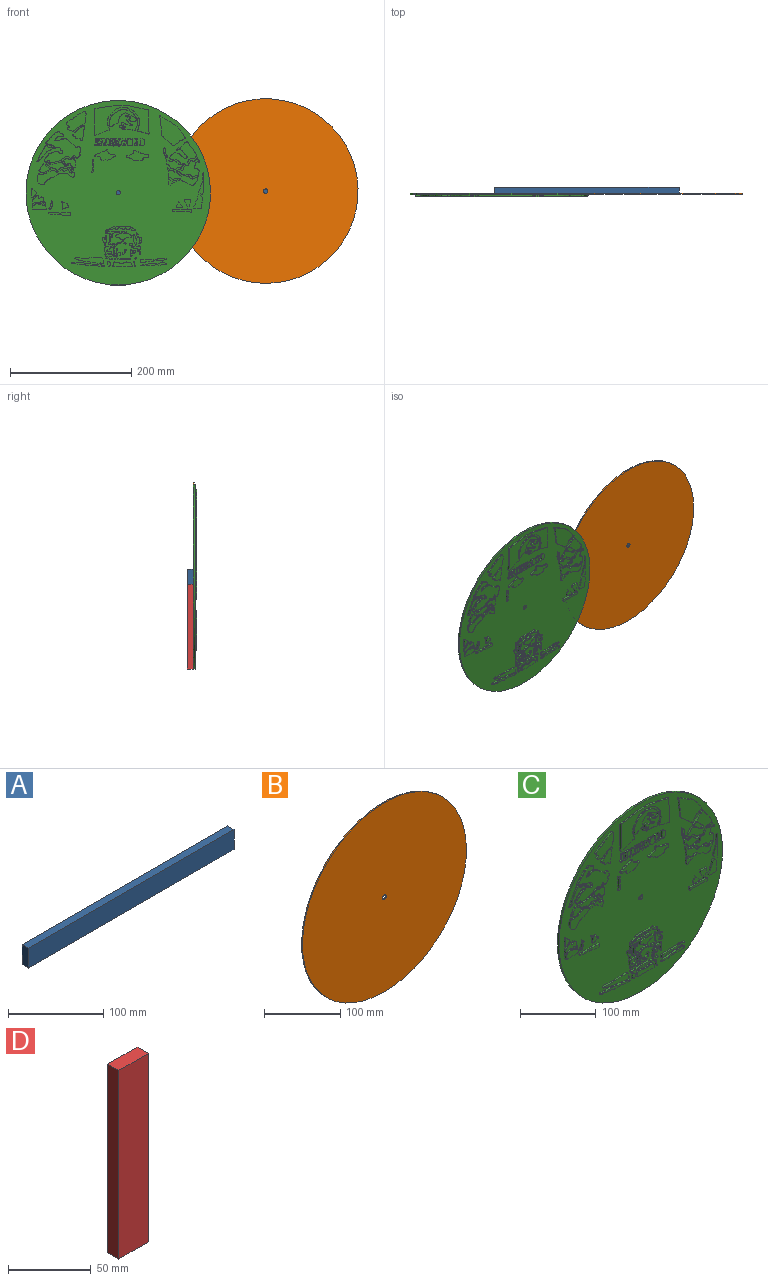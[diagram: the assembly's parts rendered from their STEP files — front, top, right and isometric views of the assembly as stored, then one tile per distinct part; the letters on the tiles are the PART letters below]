
ASSEMBLY  parts=4 mates=5
PART A: 6 faces, bbox 304.8x9.5x25.4 mm
  f0: plane 25.4x9.53mm, normal (1,0,0), area 241.9mm2, adj f1,f3,f4,f5
  f1: plane 304.8x9.53mm, normal (0,0,1), area 2903.2mm2, adj f0,f2,f4,f5
  f2: plane 25.4x9.53mm, normal (-1,0,0), area 241.9mm2, adj f1,f3,f4,f5
  f3: plane 304.8x9.53mm, normal (0,0,-1), area 2903.2mm2, adj f0,f2,f4,f5
  f4: plane 304.8x25.4mm, normal (0,-1,0), area 7741.9mm2, adj f0,f1,f2,f3
  f5: plane 304.8x25.4mm, normal (0,1,0), area 7741.9mm2, adj f0,f1,f2,f3
PART B: 4 faces, bbox 304.8x1.6x304.8 mm
  f0: cylinder r=3.63mm len=7.26mm, axis (0,1,0), area 36.2mm2, adj f2,f3
  f1: cylinder r=152.4mm len=304.8mm, axis (0,1,0), area 1520.1mm2, adj f2,f3
  f2: plane 304.8x304.8mm, normal (0,-1,0), area 72924.4mm2, adj f0,f1
  f3: plane 304.8x304.8mm, normal (0,1,0), area 72924.4mm2, adj f0,f1
PART C: 236 faces, bbox 304.8x5.5x304.8 mm
  f0: cylinder r=3.66mm len=7.32mm, axis (0,1,0), area 67.5mm2, adj f2,f164
  f1: cylinder r=152.4mm len=304.8mm, axis (0,1,0), area 2810.4mm2, adj f2,f164
  f2: plane 304.8x304.8mm, normal (0,1,0), area 72923.8mm2, adj f0,f1
  f3: plane 5.9x3.39mm, normal (-0.87,0,0.5), area 17.3mm2, adj f4,f163,f164,f235
  f4: plane 7.98x6.67mm, normal (0.77,0,0.64), area 26.4mm2, adj f3,f5,f164,f235
  f5: plane 2.54x1.53mm, normal (1,0,0), area 3.9mm2, adj f4,f6,f164,f235
  f6: plane 10.06x2.54mm, normal (0,0,-1), area 25.5mm2, adj f5,f163,f164,f235
  f7: plane 2.73x2.54mm, normal (0.78,0,-0.62), area 8.9mm2, adj f8,f93,f164,f173
  f8: plane 2.73x2.54mm, normal (-1,0,0), area 6.9mm2, adj f7,f9,f164,f173
  f9: plane 2.54x2.05mm, normal (-0.77,0,-0.64), area 6.8mm2, adj f8,f10,f164,f173
  f10: plane 4.07x2.54mm, normal (-0.88,0,-0.48), area 11.8mm2, adj f9,f11,f164,f173
  f11: plane 2.54x1.86mm, normal (-0.77,0,-0.64), area 6.2mm2, adj f10,f12,f164,f173
  f12: plane 4.37x2.54mm, normal (-1,0,0), area 11.1mm2, adj f11,f13,f164,f173
  f13: plane 10.3x2.54mm, normal (0,0,1), area 26.2mm2, adj f12,f14,f164,f173
  f14: plane 5.36x2.54mm, normal (1,0,0), area 13.6mm2, adj f13,f15,f164,f173
  f15: plane 3.28x2.54mm, normal (0.91,0,-0.42), area 9.2mm2, adj f14,f93,f164,f173
  f16: plane 4.25x2.54mm, normal (-0.23,0,0.97), area 11.1mm2, adj f17,f94,f164,f172
  f17: plane 2.54x2.01mm, normal (1,0,0), area 5.1mm2, adj f16,f18,f164,f172
  f18: plane 2.54x1.4mm, normal (-0.25,0,-0.97), area 3.7mm2, adj f17,f19,f164,f172
  f19: plane 3.17x2.54mm, normal (0.36,0,-0.93), area 8.6mm2, adj f18,f20,f164,f172
  f20: plane 2.71x2.54mm, normal (0.42,0,-0.91), area 7.6mm2, adj f19,f21,f164,f172
  f21: plane 5.1x2.78mm, normal (0.48,0,-0.88), area 14.8mm2, adj f20,f22,f164,f172
  f22: plane 2.67x2.54mm, normal (0.64,0,-0.77), area 8.8mm2, adj f21,f23,f164,f172
  f23: plane 2.54x1.97mm, normal (-0.22,0,-0.98), area 5.1mm2, adj f22,f24,f164,f172
  f24: plane 2.54x0.99mm, normal (-0.62,0,-0.78), area 3.2mm2, adj f23,f25,f164,f172
  f25: plane 9.26x2.54mm, normal (-1,0,0), area 23.5mm2, adj f24,f26,f164,f172
  f26: plane 2.54x2.4mm, normal (0.25,0,0.97), area 6.3mm2, adj f25,f27,f164,f172
  f27: plane 2.54x1.35mm, normal (0.77,0,0.64), area 4.5mm2, adj f26,f28,f164,f172
  f28: plane 3.04x2.54mm, normal (0.62,0,0.78), area 9.9mm2, adj f27,f29,f164,f172
  f29: plane 2.54x1.39mm, normal (-0.64,0,0.77), area 4.6mm2, adj f28,f30,f164,f172
  f30: plane 3.3x2.54mm, normal (-0.25,0,0.97), area 8.7mm2, adj f29,f94,f164,f172
  f31: extruded ~11.37x6.92mm, area 47.7mm2, adj f32,f95,f164,f171
  f32: plane 11.22x2.54mm, normal (-1,0,0), area 28.5mm2, adj f31,f95,f164,f171
  f33: plane 11.15x2.54mm, normal (-1,0,0), area 28.3mm2, adj f34,f157,f164,f170
  f34: plane 2.54x2.08mm, normal (0,0,1), area 5.3mm2, adj f33,f35,f164,f170
  f35: plane 8.96x2.54mm, normal (1,0,0), area 22.7mm2, adj f34,f36,f164,f170
  f36: plane 4.28x2.54mm, normal (0,0,1), area 10.9mm2, adj f35,f37,f164,f170
  f37: plane 2.54x2.19mm, normal (1,0,0), area 5.6mm2, adj f36,f157,f164,f170
  f38: plane 11.65x2.54mm, normal (-1,0,0), area 29.6mm2, adj f39,f158,f164,f169
  f39: plane 3.17x2.54mm, normal (0,0,1), area 8mm2, adj f38,f40,f164,f169
  f40: extruded ~6.75x2.78mm, area 21.1mm2, adj f39,f41,f164,f169
  f41: plane 2.54x1.4mm, normal (0.99,0,0.16), area 3.6mm2, adj f40,f42,f164,f169
  f42: plane 3.16x2.54mm, normal (0.97,0,0.25), area 8.3mm2, adj f41,f43,f164,f169
  f43: plane 2.54x1.04mm, normal (0.33,0,-0.94), area 2.8mm2, adj f42,f44,f164,f169
  f44: plane 2.54x0.52mm, normal (0.38,0,-0.93), area 1.4mm2, adj f43,f45,f164,f169
  f45: plane 3.29x2.54mm, normal (-0.93,0,-0.38), area 9mm2, adj f44,f46,f164,f169
  f46: plane 2.54x0.36mm, normal (0,0,-1), area 0.9mm2, adj f45,f47,f164,f169
  f47: plane 2.54x0.18mm, normal (0.68,0,-0.73), area 0.6mm2, adj f46,f48,f164,f169
  f48: plane 2.54x0.41mm, normal (0.9,0,-0.43), area 1.1mm2, adj f47,f49,f164,f169
  f49: plane 2.54x2.48mm, normal (1,0,0.06), area 6.3mm2, adj f48,f158,f164,f169
  f50: plane 11.36x2.57mm, normal (-0.98,0,-0.22), area 29.6mm2, adj f51,f159,f164,f168
  f51: plane 2.54x2.41mm, normal (-0.13,0,0.99), area 6.2mm2, adj f50,f52,f164,f168
  f52: plane 4.78x2.54mm, normal (0.97,0,0.22), area 12.4mm2, adj f51,f53,f164,f168
  f53: plane 2.54x0.24mm, normal (0.89,0,0.46), area 0.7mm2, adj f52,f54,f164,f168
  f54: plane 2.54x0.16mm, normal (-0.21,0,0.98), area 0.4mm2, adj f53,f55,f164,f168
  f55: plane 2.67x2.54mm, normal (-0.98,0,0.21), area 6.9mm2, adj f54,f56,f164,f168
  f56: plane 2.54x2.16mm, normal (0,0,1), area 5.5mm2, adj f55,f57,f164,f168
  f57: plane 2.67x2.54mm, normal (0.97,0,0.22), area 7mm2, adj f56,f58,f164,f168
  f58: plane 2.54x0.2mm, normal (0.4,0,0.92), area 0.6mm2, adj f57,f59,f164,f168
  f59: plane 2.54x0.18mm, normal (-0.92,0,0.4), area 0.5mm2, adj f58,f60,f164,f168
  f60: plane 4.97x2.54mm, normal (-0.97,0,0.22), area 13mm2, adj f59,f61,f164,f168
  f61: plane 2.54x2.31mm, normal (0.22,0,0.97), area 6mm2, adj f60,f62,f164,f168
  f62: plane 11.19x2.58mm, normal (0.97,0,-0.22), area 29.2mm2, adj f61,f63,f164,f168
  f63: plane 2.54x1mm, normal (-0.02,0,-1), area 2.5mm2, adj f62,f64,f164,f168
  f64: plane 2.54x0.18mm, normal (0.24,0,-0.97), area 0.5mm2, adj f63,f65,f164,f168
  f65: plane 2.54x0.83mm, normal (0,0,-1), area 2.1mm2, adj f64,f66,f164,f168
  f66: plane 3.74x2.54mm, normal (-0.98,0,-0.2), area 9.7mm2, adj f65,f67,f164,f168
  f67: plane 2.54x0.2mm, normal (0,0,-1), area 0.5mm2, adj f66,f68,f164,f168
  f68: plane 3.76x2.54mm, normal (0.97,0,-0.23), area 9.8mm2, adj f67,f159,f164,f168
  f69: plane 2.54x2.46mm, normal (0,0,-1), area 6.2mm2, adj f70,f160,f164,f167
  f70: plane 11.34x2.54mm, normal (-1,0,0), area 28.8mm2, adj f69,f71,f164,f167
  f71: plane 2.54x2.46mm, normal (0,0,1), area 6.2mm2, adj f70,f160,f164,f167
  f72: plane 6.45x3.83mm, normal (-0.51,0,-0.86), area 19mm2, adj f73,f161,f164,f166
  f73: plane 2.54x1.64mm, normal (-1,0,-0.07), area 4.2mm2, adj f72,f74,f164,f166
  f74: plane 9.62x3.28mm, normal (-0.95,0,0.32), area 25.8mm2, adj f73,f75,f164,f166
  f75: plane 5.25x2.54mm, normal (-0.94,0,0.35), area 14.2mm2, adj f74,f76,f164,f166
  f76: plane 6.56x2.54mm, normal (-1,0,0), area 16.7mm2, adj f75,f77,f164,f166
  f77: plane 4.92x2.54mm, normal (-0.97,0,0.25), area 12.9mm2, adj f76,f78,f164,f166
  f78: plane 4.18x2.54mm, normal (-1,0,0), area 10.6mm2, adj f77,f79,f164,f166
  f79: plane 2.54x1.06mm, normal (-0.78,0,0.62), area 3.5mm2, adj f78,f80,f164,f166
  f80: plane 33.75x2.54mm, normal (1,0,0), area 85.7mm2, adj f79,f81,f164,f166
  f81: plane 2.54x1.01mm, normal (0.78,0,-0.62), area 3.3mm2, adj f80,f161,f164,f166
  f82: plane 12.35x2.54mm, normal (0,0,-1), area 31.4mm2, adj f83,f162,f164,f165
  f83: plane 2.73x2.54mm, normal (-0.99,0,-0.11), area 7mm2, adj f82,f84,f164,f165
  f84: plane 3.39x2.71mm, normal (-0.78,0,0.62), area 11mm2, adj f83,f85,f164,f165
  f85: plane 4.59x2.54mm, normal (-0.97,0,0.25), area 12.1mm2, adj f84,f86,f164,f165
  f86: plane 6.01x2.71mm, normal (-0.91,0,0.41), area 16.7mm2, adj f85,f87,f164,f165
  f87: plane 3.19x2.54mm, normal (-1,0,0), area 8.1mm2, adj f86,f88,f164,f165
  f88: plane 2.54x2.48mm, normal (-0.78,0,0.62), area 8.1mm2, adj f87,f89,f164,f165
  f89: plane 6x4.8mm, normal (0.62,0,0.78), area 19.5mm2, adj f88,f90,f164,f165
  f90: plane 7.57x2.54mm, normal (1,0,0), area 19.2mm2, adj f89,f91,f164,f165
  f91: plane 2.54x1.39mm, normal (0.78,0,-0.62), area 4.5mm2, adj f90,f92,f164,f165
  f92: plane 7.6x2.54mm, normal (1,0,0), area 19.3mm2, adj f91,f162,f164,f165
  f93: plane 3.72x2.54mm, normal (0.96,0,-0.28), area 9.8mm2, adj f7,f15,f164,f173
  f94: plane 2.54x2.47mm, normal (0,0,1), area 6.3mm2, adj f16,f30,f164,f172
  f95: plane 2.54x2.38mm, normal (0,0,1), area 6mm2, adj f31,f32,f164,f171
  f96: extruded ~32.51x4.58mm, area 186.9mm2, adj f164,f174
  f97: extruded ~37.04x31.29mm, area 344.8mm2, adj f164,f175
  f98: extruded ~44.13x38.31mm, area 445.3mm2, adj f164,f176
  f99: extruded ~8.93x3.35mm, area 55.3mm2, adj f164,f177
  f100: extruded ~89.33x49.04mm, area 790.3mm2, adj f164,f178
  f101: extruded ~46.43x33.83mm, area 685.8mm2, adj f164,f179
  f102: extruded ~3.55x3.54mm, area 29.3mm2, adj f164,f180
  f103: extruded ~34.23x16.89mm, area 215.1mm2, adj f164,f181
  f104: extruded ~21.28x3.52mm, area 118.2mm2, adj f164,f182
  f105: extruded ~32.9x32.09mm, area 240.5mm2, adj f164,f183
  f106: extruded ~60.09x49.9mm, area 712.7mm2, adj f164,f184
  f107: extruded ~19.64x17.49mm, area 186.5mm2, adj f164,f185
  f108: extruded ~61.86x24.09mm, area 384.6mm2, adj f164,f186
  f109: extruded ~21.68x14.32mm, area 200.5mm2, adj f164,f187
  f110: extruded ~14.51x6.14mm, area 93mm2, adj f164,f188
  f111: extruded ~36.87x4.93mm, area 204.5mm2, adj f164,f189
  f112: extruded ~54.01x6.78mm, area 293.5mm2, adj f164,f190
  f113: extruded ~42.68x6.61mm, area 235.2mm2, adj f164,f191
  f114: extruded ~8.89x2.6mm, area 51.6mm2, adj f164,f192
  f115: extruded ~31.99x7.82mm, area 196.9mm2, adj f164,f193
  f116: extruded ~40.93x2.86mm, area 226.7mm2, adj f164,f194
  f117: extruded ~2.95x2.67mm, area 23.7mm2, adj f164,f195
  f118: extruded ~18.41x7.53mm, area 112.1mm2, adj f164,f196
  f119: extruded ~11.61x7.93mm, area 86.5mm2, adj f164,f197
  f120: extruded ~9.28x6.73mm, area 65.2mm2, adj f164,f198
  f121: extruded ~5.97x3.23mm, area 43mm2, adj f164,f199
  f122: extruded ~18.12x5.24mm, area 103.5mm2, adj f164,f200
  f123: extruded ~4.17x2.82mm, area 30mm2, adj f164,f201
  f124: extruded ~40.28x25.27mm, area 340.4mm2, adj f164,f202
  f125: extruded ~46.16x6.36mm, area 275mm2, adj f164,f203
  f126: extruded ~11.39x4.34mm, area 74.1mm2, adj f164,f204
  f127: extruded ~11.92x7.13mm, area 138.7mm2, adj f164,f205
  f128: extruded ~17.83x12.22mm, area 277.6mm2, adj f164,f206
  f129: extruded ~12.34x4.61mm, area 77.8mm2, adj f164,f207
  f130: extruded ~12.14x5.21mm, area 80.3mm2, adj f164,f208
  f131: extruded ~11.75x8.92mm, area 82.8mm2, adj f164,f209
  f132: extruded ~4.81x2.54mm, area 28.3mm2, adj f164,f210
  f133: extruded ~17.57x3mm, area 96.1mm2, adj f164,f211
  f134: extruded ~26.66x10.32mm, area 156.3mm2, adj f164,f212
  f135: extruded ~17.79x8.41mm, area 120.5mm2, adj f164,f213
  f136: extruded ~15.6x14.76mm, area 162.2mm2, adj f164,f214
  f137: extruded ~5.51x3.26mm, area 41.3mm2, adj f164,f215
  f138: extruded ~6.86x2.54mm, area 42.4mm2, adj f164,f216
  f139: extruded ~20.88x16.43mm, area 345.9mm2, adj f164,f217
  f140: extruded ~8.74x4.45mm, area 57.3mm2, adj f164,f218
  f141: extruded ~2.78x2.61mm, area 21.5mm2, adj f164,f219
  f142: extruded ~41.31x7.06mm, area 236.4mm2, adj f164,f220
  f143: extruded ~46.99x9.32mm, area 275.7mm2, adj f164,f221
  f144: extruded ~11.5x11.42mm, area 101.8mm2, adj f164,f222
  f145: extruded ~22.3x11.29mm, area 145.2mm2, adj f164,f223
  f146: extruded ~14.73x7.75mm, area 95mm2, adj f164,f224
  f147: extruded ~19.31x14.41mm, area 136mm2, adj f164,f225
  f148: extruded ~43.41x15.28mm, area 289mm2, adj f164,f226
  f149: extruded ~27.63x25.82mm, area 204.7mm2, adj f164,f227
  f150: extruded ~24.49x18.44mm, area 188.6mm2, adj f164,f228
  f151: extruded ~36.61x16.96mm, area 227.8mm2, adj f164,f229
  f152: extruded ~3.25x2.76mm, area 23.9mm2, adj f164,f230
  f153: extruded ~48.67x42.38mm, area 362mm2, adj f164,f231
  f154: extruded ~8.19x5.88mm, area 64.7mm2, adj f164,f232
  f155: extruded ~28.6x15.3mm, area 206.9mm2, adj f164,f233
  f156: extruded ~49.32x28.56mm, area 329.5mm2, adj f164,f234
  f157: plane 6.36x2.54mm, normal (0,0,-1), area 16.2mm2, adj f33,f37,f164,f170
  f158: plane 2.54x2.25mm, normal (0,0,-1), area 5.7mm2, adj f38,f49,f164,f169
  f159: plane 2.54x1.89mm, normal (0,0,-1), area 4.8mm2, adj f50,f68,f164,f168
  f160: plane 11.34x2.54mm, normal (1,0,0), area 28.8mm2, adj f69,f71,f164,f167
  f161: plane 2.54x2.3mm, normal (1,0,0), area 5.8mm2, adj f72,f81,f164,f166
  f162: plane 2.54x1.04mm, normal (0.78,0,-0.62), area 3.4mm2, adj f82,f92,f164,f165
  f163: plane 3.61x2.54mm, normal (-1,0,0), area 9.2mm2, adj f3,f6,f164,f235
  f164: plane 304.8x304.8mm, normal (0,-1,0), area 59386.4mm2, adj f0,f1,f3,f4,f5,f6,f7,f8
  f165: plane 22.4x14.6mm, normal (0,-1,0), area 210mm2, adj f82,f83,f84,f85,f86,f87,f88,f89
  f166: plane 37.05x7.37mm, normal (0,-1,0), area 121.8mm2, adj f72,f73,f74,f75,f76,f77,f78,f79
  f167: plane 11.34x2.46mm, normal (0,-1,0), area 27.9mm2, adj f69,f70,f71,f160
  f168: plane 11.77x10.87mm, normal (0,-1,0), area 75.7mm2, adj f50,f51,f52,f53,f54,f55,f56,f57
  f169: plane 11.88x5.97mm, normal (0,-1,0), area 57.7mm2, adj f38,f39,f40,f41,f42,f43,f44,f45
  f170: plane 11.15x6.36mm, normal (0,-1,0), area 32.6mm2, adj f33,f34,f35,f36,f37,f157
  f171: plane 11.45x7mm, normal (0,-1,0), area 67.2mm2, adj f31,f32,f95
  f172: plane 17.99x10.5mm, normal (0,-1,0), area 78.6mm2, adj f16,f17,f18,f19,f20,f21,f22,f23
  f173: plane 15.08x10.3mm, normal (0,-1,0), area 98.2mm2, adj f7,f8,f9,f10,f11,f12,f13,f14
  f174: plane 32.93x5.27mm, normal (0,-1,0), area 122.5mm2, adj f96
  f175: plane 39.21x32.09mm, normal (0,-1,0), area 514.9mm2, adj f97
  f176: plane 44.76x38.5mm, normal (0,-1,0), area 799.7mm2, adj f98
  f177: plane 9.11x3.53mm, normal (0,-1,0), area 21mm2, adj f99
  f178: plane 91.08x49.51mm, normal (0,-1,0), area 1971.8mm2, adj f100
  f179: plane 46.71x34.4mm, normal (0,-1,0), area 579.6mm2, adj f101
  f180: plane 3.62x3.61mm, normal (0,-1,0), area 7.1mm2, adj f102
  f181: plane 34.67x17.68mm, normal (0,-1,0), area 310.7mm2, adj f103
  f182: plane 21.61x3.73mm, normal (0,-1,0), area 57.9mm2, adj f104
  f183: plane 33.1x32.96mm, normal (0,-1,0), area 620.5mm2, adj f105
  f184: plane 61.2x53.07mm, normal (0,-1,0), area 1776.8mm2, adj f106
  f185: plane 20.01x17.98mm, normal (0,-1,0), area 196.7mm2, adj f107
  f186: plane 62.1x25.64mm, normal (0,-1,0), area 513.1mm2, adj f108
  f187: plane 21.88x14.76mm, normal (0,-1,0), area 160.2mm2, adj f109
  f188: plane 14.66x6.34mm, normal (0,-1,0), area 32.1mm2, adj f110
  f189: plane 37.06x5.21mm, normal (0,-1,0), area 125.3mm2, adj f111
  f190: plane 55.6x7.2mm, normal (0,-1,0), area 160.1mm2, adj f112
  f191: plane 43.52x6.8mm, normal (0,-1,0), area 128.5mm2, adj f113
  f192: plane 9.08x2.75mm, normal (0,-1,0), area 11.1mm2, adj f114
  f193: plane 32.63x8.14mm, normal (0,-1,0), area 217mm2, adj f115
  f194: plane 41.57x2.99mm, normal (0,-1,0), area 90.3mm2, adj f116
  f195: plane 3x2.73mm, normal (0,-1,0), area 5.1mm2, adj f117
  f196: plane 18.69x7.67mm, normal (0,-1,0), area 35.6mm2, adj f118
  f197: plane 11.91x8.22mm, normal (0,-1,0), area 38.5mm2, adj f119
  f198: plane 9.59x6.92mm, normal (0,-1,0), area 25.7mm2, adj f120
  f199: plane 6.16x3.39mm, normal (0,-1,0), area 17mm2, adj f121
  f200: plane 18.39x5.38mm, normal (0,-1,0), area 61mm2, adj f122
  f201: plane 4.26x2.91mm, normal (0,-1,0), area 8.5mm2, adj f123
  f202: plane 40.4x25.61mm, normal (0,-1,0), area 191.9mm2, adj f124
  f203: plane 46.31x6.56mm, normal (0,-1,0), area 164.2mm2, adj f125
  f204: plane 11.49x4.37mm, normal (0,-1,0), area 31.3mm2, adj f126
  f205: plane 11.98x7.18mm, normal (0,-1,0), area 56.6mm2, adj f127
  f206: plane 17.92x12.45mm, normal (0,-1,0), area 156.2mm2, adj f128
  f207: plane 12.44x4.74mm, normal (0,-1,0), area 34.8mm2, adj f129
  f208: plane 12.17x5.23mm, normal (0,-1,0), area 32.1mm2, adj f130
  f209: plane 11.8x8.94mm, normal (0,-1,0), area 88.2mm2, adj f131
  f210: plane 4.88x2.07mm, normal (0,-1,0), area 6.9mm2, adj f132
  f211: plane 17.71x3.09mm, normal (0,-1,0), area 36.2mm2, adj f133
  f212: plane 26.81x10.64mm, normal (0,-1,0), area 174.3mm2, adj f134
  f213: plane 18.18x8.53mm, normal (0,-1,0), area 50mm2, adj f135
  f214: plane 15.82x14.92mm, normal (0,-1,0), area 67.3mm2, adj f136
  f215: plane 5.59x3.34mm, normal (0,-1,0), area 15.5mm2, adj f137
  f216: plane 6.97x2.53mm, normal (0,-1,0), area 14mm2, adj f138
  f217: plane 21.77x16.59mm, normal (0,-1,0), area 135.9mm2, adj f139
  f218: plane 9.02x4.62mm, normal (0,-1,0), area 28.4mm2, adj f140
  f219: plane 2.9x2.69mm, normal (0,-1,0), area 2.9mm2, adj f141
  f220: plane 42.12x7.48mm, normal (0,-1,0), area 140.9mm2, adj f142
  f221: plane 47.68x9.51mm, normal (0,-1,0), area 293.4mm2, adj f143
  f222: plane 11.79x11.7mm, normal (0,-1,0), area 73.1mm2, adj f144
  f223: plane 22.58x11.46mm, normal (0,-1,0), area 189.7mm2, adj f145
  f224: plane 14.91x7.93mm, normal (0,-1,0), area 66.6mm2, adj f146
  f225: plane 19.66x14.73mm, normal (0,-1,0), area 148.5mm2, adj f147
  f226: plane 44.18x16.16mm, normal (0,-1,0), area 251mm2, adj f148
  f227: plane 27.72x26.87mm, normal (0,-1,0), area 182.1mm2, adj f149
  f228: plane 24.93x18.82mm, normal (0,-1,0), area 262.4mm2, adj f150
  f229: plane 37.02x17.16mm, normal (0,-1,0), area 359.3mm2, adj f151
  f230: plane 3.33x2.84mm, normal (0,-1,0), area 5.3mm2, adj f152
  f231: plane 49.77x43.47mm, normal (0,-1,0), area 1089.2mm2, adj f153
  f232: plane 8.35x6.03mm, normal (0,-1,0), area 17.9mm2, adj f154
  f233: plane 28.77x15.84mm, normal (0,-1,0), area 237.5mm2, adj f155
  f234: plane 49.81x29.84mm, normal (0,-1,0), area 480.5mm2, adj f156
  f235: plane 10.06x9.51mm, normal (0,-1,0), area 59mm2, adj f3,f4,f5,f6,f163
PART D: 6 faces, bbox 25.4x9.5x139.7 mm
  f0: plane 25.4x9.53mm, normal (0,0,1), area 241.9mm2, adj f1,f3,f4,f5
  f1: plane 139.7x9.53mm, normal (-1,0,0), area 1330.6mm2, adj f0,f2,f4,f5
  f2: plane 25.4x9.53mm, normal (0,0,-1), area 241.9mm2, adj f1,f3,f4,f5
  f3: plane 139.7x9.53mm, normal (1,0,0), area 1330.6mm2, adj f0,f2,f4,f5
  f4: plane 139.7x25.4mm, normal (0,-1,0), area 3548.4mm2, adj f0,f1,f2,f3
  f5: plane 139.7x25.4mm, normal (0,1,0), area 3548.4mm2, adj f0,f1,f2,f3
PLACE A t=(-11.19,3.76,8.19)mm fixed
PLACE B t=(92.78,-5.77,10.88)mm
PLACE C t=(-150.89,-5.77,8.19)mm
PLACE D t=(-150.89,3.76,-74.36)mm
MATE planar D.f4 <-> C.f1  axis (0,-1,0) through (-150.89,-5.77,-74.36)mm
MATE planar D.f1 <-> A.f2  axis (-1,0,0) through (-163.59,-1,-74.36)mm
MATE planar A.f3 <-> D.f0  axis (0,0,-1) through (-11.19,-1,-4.51)mm
MATE planar D.f4 <-> A.f4  axis (0,-1,0) through (-150.89,-5.77,-4.51)mm
MATE planar B.f1 <-> A.f4  axis (0,1,0) through (92.78,-5.77,10.88)mm
